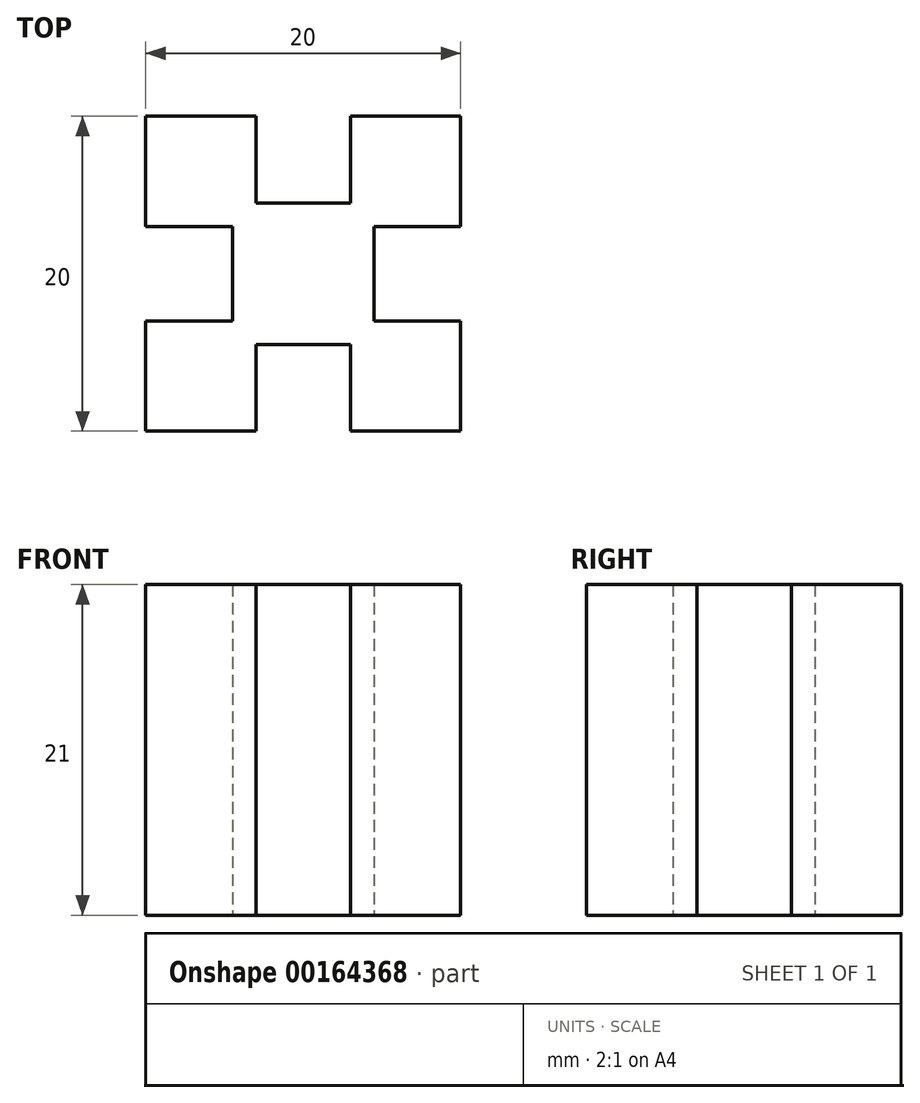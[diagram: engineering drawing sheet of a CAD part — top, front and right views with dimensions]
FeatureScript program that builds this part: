
annotation { "Feature Type Name" : "Feature", "Feature Type Description" : "" }
export const myFeature = defineFeature(function(context is Context, id is Id, definition is map)
    precondition{}
    {
        {
            var Q0;
            Q0=qCreatedBy(makeId("Top.planeOp"),FACE);
            var sketch = newSketch(context, id + "F0", { "sketchPlane" : qUnion([Q0])});
            skLineSegment(sketch, "E0.bottom", {"start": v(0, 0) * mm, "end": v(20, 0) * mm});
            skLineSegment(sketch, "E0.top", {"start": v(0, 20) * mm, "end": v(20, 20) * mm});
            skLineSegment(sketch, "E0.left", {"start": v(0, 0) * mm, "end": v(0, 20) * mm});
            skLineSegment(sketch, "E0.right", {"start": v(20, 0) * mm, "end": v(20, 20) * mm});
            skLineSegment(sketch, "E1.bottom", {"start": v(7, 20) * mm, "end": v(13, 20) * mm});
            skLineSegment(sketch, "E1.top", {"start": v(7, 14.5) * mm, "end": v(13, 14.5) * mm});
            skLineSegment(sketch, "E1.left", {"start": v(7, 20) * mm, "end": v(7, 14.5) * mm});
            skLineSegment(sketch, "E1.right", {"start": v(13, 20) * mm, "end": v(13, 14.5) * mm});
            skLineSegment(sketch, "E2.bottom", {"start": v(20, 13) * mm, "end": v(14.5, 13) * mm});
            skLineSegment(sketch, "E2.top", {"start": v(20, 7) * mm, "end": v(14.5, 7) * mm});
            skLineSegment(sketch, "E2.left", {"start": v(20, 13) * mm, "end": v(20, 7) * mm});
            skLineSegment(sketch, "E2.right", {"start": v(14.5, 13) * mm, "end": v(14.5, 7) * mm});
            skLineSegment(sketch, "E3.bottom", {"start": v(13, 0) * mm, "end": v(7, 0) * mm});
            skLineSegment(sketch, "E3.top", {"start": v(13, 5.5) * mm, "end": v(7, 5.5) * mm});
            skLineSegment(sketch, "E3.left", {"start": v(13, 0) * mm, "end": v(13, 5.5) * mm});
            skLineSegment(sketch, "E3.right", {"start": v(7, 0) * mm, "end": v(7, 5.5) * mm});
            skLineSegment(sketch, "E4.bottom", {"start": v(0, 7) * mm, "end": v(5.5, 7) * mm});
            skLineSegment(sketch, "E4.top", {"start": v(0, 13) * mm, "end": v(5.5, 13) * mm});
            skLineSegment(sketch, "E4.left", {"start": v(0, 7) * mm, "end": v(0, 13) * mm});
            skLineSegment(sketch, "E4.right", {"start": v(5.5, 7) * mm, "end": v(5.5, 13) * mm});
            skSolve(sketch);
        }
        {
            var Q0;
            Q0=makeQuery(id+"F0.imprint","IMPRINT",FACE,{"disambiguationData":[TD([[makeQuery(id+"F0.imprint","IMPRINT",EDGE,{"derivedFrom":sQuery(id+"F0.wireOp",EDGE,"E1.top")}),-1.0]])]});
            extrude(context, id + "F1", {"entities" : qUnion([Q0]), "depth" : 21 * mm});
        }
        {
            var Q0;
            Q0=makeQuery(id+"F1.opExtrude","SWEPT_FACE",FACE,{"disambiguationData":[OSD([sQuery(id+"F0.wireOp",EDGE,"E3.top")])]});
            var sketch = newSketch(context, id + "F2", { "sketchPlane" : qUnion([Q0])});
            skCircle(sketch, "E5", {"center": v(10, 70) * mm, "radius": 2.5 * mm});
            skPoint(sketch, "E5.centerSnap0", {"position": v(10, 0) * mm});
            skSolve(sketch);
        }
        {
            var Q0;
            Q0=qSketchRegion(id+"F2",true);
            extrude(context, id + "F3", {"entities" : qUnion([Q0]), "operationType" : NewBodyOperationType.REMOVE, "oppositeDirection" : true, "depth" : 25 * mm});
        }
        {
            var Q0;
            Q0=makeQuery(id+"F1.opExtrude","SWEPT_FACE",FACE,{"disambiguationData":[OSD([sQuery(id+"F0.wireOp",EDGE,"E2.right")])]});
            var sketch = newSketch(context, id + "F4", { "sketchPlane" : qUnion([Q0])});
            skCircle(sketch, "E6", {"center": v(10, 70) * mm, "radius": 2.5 * mm});
            skPoint(sketch, "E6.centerSnap0", {"position": v(10, 0) * mm});
            skSolve(sketch);
        }
        {
            var Q0;
            Q0=qSketchRegion(id+"F4",true);
            extrude(context, id + "F5", {"entities" : qUnion([Q0]), "operationType" : NewBodyOperationType.REMOVE, "oppositeDirection" : true, "depth" : 25 * mm});
        }
    });
